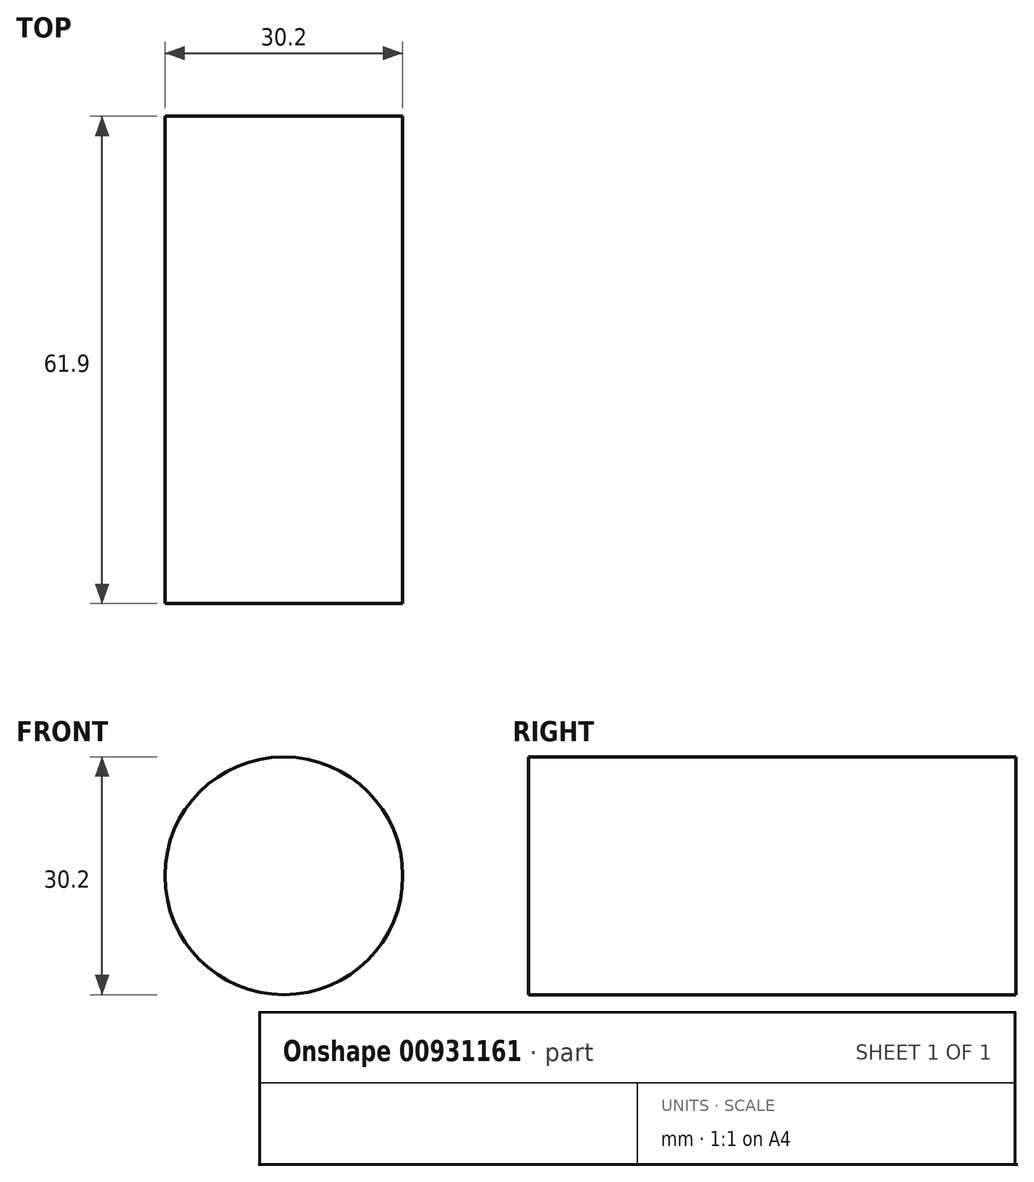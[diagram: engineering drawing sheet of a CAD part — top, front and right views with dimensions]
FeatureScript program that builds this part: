
annotation { "Feature Type Name" : "Feature", "Feature Type Description" : "" }
export const myFeature = defineFeature(function(context is Context, id is Id, definition is map)
    precondition{}
    {
        {
            var Q0;
            Q0=qCreatedBy(makeId("Front.planeOp"),FACE);
            var sketch = newSketch(context, id + "F0", { "sketchPlane" : qUnion([Q0])});
            skLineSegment(sketch, "E0", {"start": v(-62.46, 53.96) * mm, "end": v(27.9, 53.96) * mm});
            skLineSegment(sketch, "E1", {"start": v(27.9, 53.96) * mm, "end": v(30.17, 24.5) * mm});
            skLineSegment(sketch, "E2", {"start": v(30.17, 24.5) * mm, "end": v(49.43, -19.4) * mm});
            skLineSegment(sketch, "E3", {"start": v(49.43, -19.4) * mm, "end": v(-43.48, -46.6) * mm});
            skLineSegment(sketch, "E4", {"start": v(-43.48, -46.6) * mm, "end": v(-62.46, 53.96) * mm});
            skCircle(sketch, "E5", {"center": v(-25.35, 16) * mm, "radius": 16.98 * mm});
            skSolve(sketch);
        }
        {
            var Q0;
            Q0=makeQuery(id+"F0.imprint","IMPRINT",FACE,{"disambiguationData":[TD([[makeQuery(id+"F0.imprint","IMPRINT",EDGE,{"derivedFrom":sQuery(id+"F0.wireOp",EDGE,"E0")}),-1.0]])]});
            extrude(context, id + "F1", {"entities" : qUnion([Q0]), "depth" : 73 * mm, "offsetDistance" : 25 * mm});
        }
        {
            var Q0;
            Q0=makeQuery(id+"F1.opExtrude","SWEPT_EDGE",EDGE,{"disambiguationData":[OSD([sQuery(id+"F0.wireOp",EDGE,"E2"),sQuery(id+"F0.wireOp",EDGE,"E3")])]});
            fillet(context, id + "F2", {"entities" : qUnion([Q0]), "radius" : 27.2 * mm, "tangentPropagation" : true, "allowEdgeOverflow" : false});
        }
        {
            var Q0;
            Q0=makeQuery(id+"F1.opExtrude","CAP_FACE",FACE,{"disambiguationData":[OSD([sQuery(id+"F0.wireOp",EDGE,"E0"),sQuery(id+"F0.wireOp",EDGE,"E1"),sQuery(id+"F0.wireOp",EDGE,"E2"),sQuery(id+"F0.wireOp",EDGE,"E3"),sQuery(id+"F0.wireOp",EDGE,"E4"),sQuery(id+"F0.wireOp",EDGE,"E5")])],"isStart":false});
            var sketch = newSketch(context, id + "F3", { "sketchPlane" : qUnion([Q0])});
            skCircle(sketch, "E6", {"center": v(11.92, 11.3) * mm, "radius": 15.1 * mm});
            skSolve(sketch);
        }
        {
            var Q0;
            Q0=makeQuery(id+"F3.imprint","IMPRINT",FACE,{"disambiguationData":[TD([[makeQuery(id+"F3.imprint","IMPRINT",EDGE,{"derivedFrom":sQuery(id+"F3.wireOp",EDGE,"E6")}),1.0]])]});
            extrude(context, id + "F4", {"entities" : qUnion([Q0]), "operationType" : NewBodyOperationType.INTERSECT, "oppositeDirection" : true, "depth" : 61.9 * mm, "offsetDistance" : 25 * mm});
        }
    });
